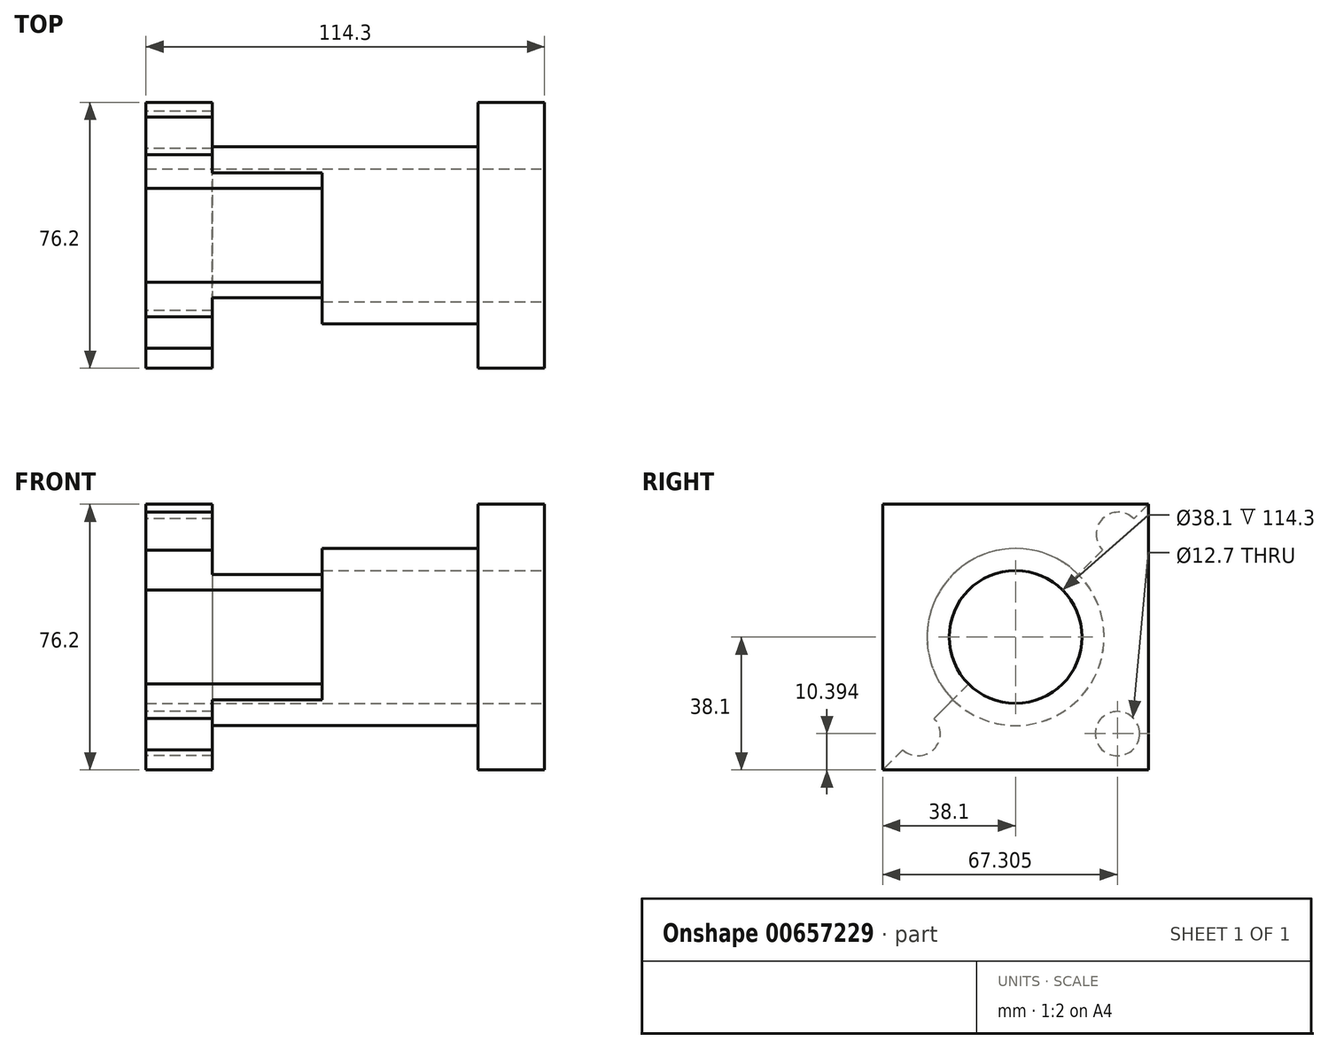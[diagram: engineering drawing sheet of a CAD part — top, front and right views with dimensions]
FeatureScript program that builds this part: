
annotation { "Feature Type Name" : "Feature", "Feature Type Description" : "" }
export const myFeature = defineFeature(function(context is Context, id is Id, definition is map)
    precondition{}
    {
        {
            var Q0;
            Q0=qCreatedBy(makeId("Right.planeOp"),FACE);
            var sketch = newSketch(context, id + "F0", { "sketchPlane" : qUnion([Q0])});
            skLineSegment(sketch, "E0.bottom", {"start": v(-38.1, 38.1) * mm, "end": v(38.1, 38.1) * mm});
            skLineSegment(sketch, "E0.top", {"start": v(-38.1, -38.1) * mm, "end": v(38.1, -38.1) * mm});
            skLineSegment(sketch, "E0.left", {"start": v(-38.1, 38.1) * mm, "end": v(-38.1, -38.1) * mm});
            skLineSegment(sketch, "E0.right", {"start": v(38.1, 38.1) * mm, "end": v(38.1, -38.1) * mm});
            skPoint(sketch, "E0.middle", {"position": v(0, 0) * mm});
            skSolve(sketch);
        }
        {
            var Q0;
            Q0=makeQuery(id+"F0.imprint","IMPRINT",FACE,{"disambiguationData":[TD([[makeQuery(id+"F0.imprint","IMPRINT",EDGE,{"derivedFrom":sQuery(id+"F0.wireOp",EDGE,"E0.bottom")}),-1.0]])]});
            extrude(context, id + "F1", {"entities" : qUnion([Q0]), "depth" : 19.05 * mm, "offsetDistance" : 25.4 * mm});
        }
        {
            var Q0;
            Q0=makeQuery(id+"F1.opExtrude","CAP_FACE",FACE,{"disambiguationData":[OSD([sQuery(id+"F0.wireOp",EDGE,"E0.bottom"),sQuery(id+"F0.wireOp",EDGE,"E0.top"),sQuery(id+"F0.wireOp",EDGE,"E0.left"),sQuery(id+"F0.wireOp",EDGE,"E0.right")])],"isStart":true});
            var sketch = newSketch(context, id + "F2", { "sketchPlane" : qUnion([Q0])});
            skCircle(sketch, "E1", {"center": v(0, 0) * mm, "radius": 25.4 * mm});
            skSolve(sketch);
        }
        {
            var Q0;
            Q0=makeQuery(id+"F2.imprint","IMPRINT",FACE,{"disambiguationData":[TD([[makeQuery(id+"F2.imprint","IMPRINT",EDGE,{"derivedFrom":sQuery(id+"F2.wireOp",EDGE,"E1")}),1.0]])]});
            extrude(context, id + "F3", {"entities" : qUnion([Q0]), "operationType" : NewBodyOperationType.ADD, "depth" : 76.2 * mm, "offsetDistance" : 25.4 * mm});
        }
        {
            var Q0;
            Q0=makeQuery(id+"F3.opExtrude","CAP_FACE",FACE,{"disambiguationData":[OSD([sQuery(id+"F2.wireOp",EDGE,"E1")])],"isStart":false});
            var sketch = newSketch(context, id + "F4", { "sketchPlane" : qUnion([Q0])});
            skLineSegment(sketch, "E2.bottom", {"start": v(38.1, 38.1) * mm, "end": v(-38.1, 38.1) * mm});
            skLineSegment(sketch, "E2.top", {"start": v(38.1, -38.1) * mm, "end": v(-38.1, -38.1) * mm});
            skLineSegment(sketch, "E2.left", {"start": v(38.1, 38.1) * mm, "end": v(38.1, -38.1) * mm});
            skLineSegment(sketch, "E2.right", {"start": v(-38.1, 38.1) * mm, "end": v(-38.1, -38.1) * mm});
            skPoint(sketch, "E2.middle", {"position": v(0, 0) * mm});
            skSolve(sketch);
        }
        {
            var Q0;
            Q0=makeQuery(id+"F4.imprint","IMPRINT",FACE,{"disambiguationData":[TD([[makeQuery(id+"F4.imprint","IMPRINT",EDGE,{"derivedFrom":sQuery(id+"F4.wireOp",EDGE,"E2.bottom")}),1.0]])]});
            extrude(context, id + "F5", {"entities" : qUnion([Q0]), "depth" : 19.05 * mm, "offsetDistance" : 25.4 * mm});
        }
        {
            var Q0;
            Q0=makeQuery(id+"F3.opExtrude","CAP_FACE",FACE,{"disambiguationData":[OSD([sQuery(id+"F2.wireOp",EDGE,"E1")])],"isStart":false});
            var sketch = newSketch(context, id + "F6", { "sketchPlane" : qUnion([Q0])});
            skCircle(sketch, "E3", {"center": v(0, 0) * mm, "radius": 25.4 * mm});
            skSolve(sketch);
        }
        {
            var Q0;
            Q0=makeQuery(id+"F6.imprint","IMPRINT",FACE,{"disambiguationData":[TD([[makeQuery(id+"F6.imprint","IMPRINT",EDGE,{"derivedFrom":sQuery(id+"F6.wireOp",EDGE,"E3")}),1.0]])]});
            extrude(context, id + "F7", {"entities" : qUnion([Q0]), "depth" : 19.05 * mm, "offsetDistance" : 25.4 * mm});
        }
        {
            var Q0;
            Q0=makeQuery(id+"F7.opExtrude","CAP_FACE",FACE,{"disambiguationData":[OSD([sQuery(id+"F6.wireOp",EDGE,"E3")])],"isStart":false});
            var sketch = newSketch(context, id + "F8", { "sketchPlane" : qUnion([Q0])});
            skCircle(sketch, "E4", {"center": v(0, 0) * mm, "radius": 19.05 * mm});
            skSolve(sketch);
        }
        {
            var Q0;
            Q0=makeQuery(id+"F1.opExtrude","CAP_FACE",FACE,{"disambiguationData":[OSD([sQuery(id+"F0.wireOp",EDGE,"E0.bottom"),sQuery(id+"F0.wireOp",EDGE,"E0.top"),sQuery(id+"F0.wireOp",EDGE,"E0.left"),sQuery(id+"F0.wireOp",EDGE,"E0.right")])],"isStart":false});
            var sketch = newSketch(context, id + "F9", { "sketchPlane" : qUnion([Q0])});
            skCircle(sketch, "E5", {"center": v(0, 0) * mm, "radius": 19.05 * mm});
            skSolve(sketch);
        }
        {
            var Q0;
            Q0=makeQuery(id+"F9.imprint","IMPRINT",FACE,{"disambiguationData":[TD([[makeQuery(id+"F9.imprint","IMPRINT",EDGE,{"derivedFrom":sQuery(id+"F9.wireOp",EDGE,"E5")}),1.0]])]});
            extrude(context, id + "F10", {"entities" : qUnion([Q0]), "operationType" : NewBodyOperationType.REMOVE, "oppositeDirection" : true, "depth" : 114.3 * mm, "offsetDistance" : 25.4 * mm});
        }
        {
            var Q0;
            Q0=makeQuery(id+"F8.imprint","IMPRINT",FACE,{"disambiguationData":[TD([[makeQuery(id+"F8.imprint","IMPRINT",EDGE,{"derivedFrom":sQuery(id+"F8.wireOp",EDGE,"E4")}),1.0]])]});
            extrude(context, id + "F11", {"entities" : qUnion([Q0]), "operationType" : NewBodyOperationType.REMOVE, "oppositeDirection" : true, "depth" : 608.08 * mm, "offsetDistance" : 25.4 * mm});
        }
        {
            var Q0;
            Q0=makeQuery(id+"F5.opExtrude","SWEPT_BODY",BODY,{"disambiguationData":[OSD([sQuery(id+"F2.wireOp",EDGE,"E1"),sQuery(id+"F4.wireOp",EDGE,"E2.bottom"),sQuery(id+"F4.wireOp",EDGE,"E2.top"),sQuery(id+"F4.wireOp",EDGE,"E2.left"),sQuery(id+"F4.wireOp",EDGE,"E2.right")])]});
            var Q1;
            Q1=makeQuery(id+"F7.opExtrude","SWEPT_BODY",BODY,{"disambiguationData":[OSD([sQuery(id+"F6.wireOp",EDGE,"E3")])]});
            var Q2;
            Q2=makeQuery(id+"F1.opExtrude","SWEPT_BODY",BODY,{"disambiguationData":[OSD([sQuery(id+"F0.wireOp",EDGE,"E0.bottom"),sQuery(id+"F0.wireOp",EDGE,"E0.top"),sQuery(id+"F0.wireOp",EDGE,"E0.left"),sQuery(id+"F0.wireOp",EDGE,"E0.right")])]});
            booleanBodies(context, id + "F12", {"operationType" : BooleanOperationType.UNION, "tools" : qUnion([Q0, Q1, Q2])});
        }
        {
            var Q0;
            Q0=makeQuery(id+"F12.opBoolean","MERGE",FACE,{"derivedFrom":[makeQuery(id+"F5.opExtrude","CAP_FACE",FACE,{"disambiguationData":[OSD([sQuery(id+"F2.wireOp",EDGE,"E1"),sQuery(id+"F4.wireOp",EDGE,"E2.bottom"),sQuery(id+"F4.wireOp",EDGE,"E2.top"),sQuery(id+"F4.wireOp",EDGE,"E2.left"),sQuery(id+"F4.wireOp",EDGE,"E2.right")])],"isStart":false}),makeQuery(id+"F7.opExtrude","CAP_FACE",FACE,{"disambiguationData":[OSD([sQuery(id+"F6.wireOp",EDGE,"E3")])],"isStart":false})]});
            var sketch = newSketch(context, id + "F13", { "sketchPlane" : qUnion([Q0])});
            skLineSegment(sketch, "E6", {"start": v(-38.1, 38.1) * mm, "end": v(38.1, -38.1) * mm});
            skCircle(sketch, "E7", {"center": v(-29.44, 29.44) * mm, "radius": 6.35 * mm});
            skCircle(sketch, "E8.0.1.0", {"center": v(-29.2, -27.7) * mm, "radius": 6.35 * mm});
            skCircle(sketch, "E8.1.0.0", {"center": v(27.7, 29.44) * mm, "radius": 6.35 * mm});
            skCircle(sketch, "E8.1.1.0", {"center": v(27.95, -27.7) * mm, "radius": 6.35 * mm});
            skLineSegment(sketch, "E8.direction1", {"start": v(-29.44, 29.44) * mm, "end": v(27.7, 29.44) * mm, "construction": true});
            skLineSegment(sketch, "E8.direction2", {"start": v(-29.44, 29.44) * mm, "end": v(-29.2, -27.7) * mm, "construction": true});
            skSolve(sketch);
        }
        {
            var Q0;
            Q0=makeQuery(id+"F13.imprint","IMPRINT",FACE,{"disambiguationData":[TD([[makeQuery(id+"F13.imprint","IMPRINT",EDGE,{"derivedFrom":sQuery(id+"F13.wireOp",EDGE,"E8.0.1.0")}),1.0]])]});
            var Q1;
            Q1=makeQuery(id+"F13.imprint","IMPRINT",FACE,{"disambiguationData":[TD([[makeQuery(id+"F13.imprint","IMPRINT",EDGE,{"derivedFrom":sQuery(id+"F13.wireOp",EDGE,"E8.1.0.0")}),1.0]])]});
            var Q2;
            {var subQ0=sQuery(id+"F13.wireOp",EDGE,"E7");var subQ1=sQuery(id+"F13.wireOp",EDGE,"E6");var subQ2=makeQuery(id+"F13.imprint","INTERSECT",VERTEX,{"disambiguationData":[OD(0.0)],"derivedFrom":[subQ1,subQ0]});Q2=makeQuery(id+"F13.imprint","IMPRINT",FACE,{"disambiguationData":[TD([[makeQuery(id+"F13.imprint","IMPRINT",EDGE,{"disambiguationData":[TD([[subQ2,-1.0]])],"derivedFrom":subQ1}),1.0]])]});}
            var Q3;
            {var subQ0=sQuery(id+"F13.wireOp",EDGE,"E8.1.1.0");var subQ1=sQuery(id+"F13.wireOp",EDGE,"E6");var subQ2=makeQuery(id+"F13.imprint","INTERSECT",VERTEX,{"disambiguationData":[OD(0.0)],"derivedFrom":[subQ1,subQ0]});Q3=makeQuery(id+"F13.imprint","IMPRINT",FACE,{"disambiguationData":[TD([[makeQuery(id+"F13.imprint","IMPRINT",EDGE,{"disambiguationData":[TD([[subQ2,-1.0]])],"derivedFrom":subQ1}),-1.0]])]});}
            var Q4;
            {var subQ0=sQuery(id+"F13.wireOp",EDGE,"E8.1.1.0");var subQ1=sQuery(id+"F13.wireOp",EDGE,"E6");var subQ2=makeQuery(id+"F13.imprint","INTERSECT",VERTEX,{"disambiguationData":[OD(0.0)],"derivedFrom":[subQ1,subQ0]});Q4=makeQuery(id+"F13.imprint","IMPRINT",FACE,{"disambiguationData":[TD([[makeQuery(id+"F13.imprint","IMPRINT",EDGE,{"disambiguationData":[TD([[subQ2,-1.0]])],"derivedFrom":subQ1}),1.0]])]});}
            extrude(context, id + "F14", {"entities" : qUnion([Q0, Q1, Q2, Q3, Q4]), "operationType" : NewBodyOperationType.REMOVE, "oppositeDirection" : true, "depth" : 50.55 * mm, "offsetDistance" : 25.4 * mm});
        }
    });
